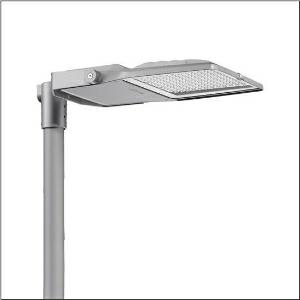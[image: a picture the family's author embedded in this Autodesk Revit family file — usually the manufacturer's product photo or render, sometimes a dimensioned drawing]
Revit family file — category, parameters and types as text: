
# Revit family: floodlight_fl_21_iq_midi___pl52_5xa7782e4d3a_8c54
name_source: partatom
category: Lighting Fixtures
units: mm (PartAtom-declared; Revit-internal decimal feet)

## family parameters
Cut with Voids When Loaded = No
Host = Face
Light Source = No
Part Type = Normal
Room Calculation Point = No
Round Connector Dimension = Use Diameter
Shared = No

## types (1)
- --- (1 x LED, 28010 lm, 208.1 W, 4000K)
    Apparent Load = 208 VA
    CIE Flux Codes = 26 60 98 100 100
    Color Rendering = 70
    Color Temperature = 4000K
    Default Elevation = 1800 mm
    Description = Floodlight FL 21 iQ midi, floodlight, primary light control with lens, of PMMA, primary optical cover: protective disc, of toughened safety glass, transparent, light distribution: PL52, light emission: direct distribution, installation type: surface-mounted, LED, High Power LED, rated luminous flux: 28.010lm, luminous efficacy: 135lm/W, light colour: 740, colour temperature: 4000K, control gear: iQ Street-Remote/DALI, control: optimised constant luminous flux control (CLO 2.0), Desk-Remote (wireless, voltage-free reading and setting of iQ features in the workshop via application-optimized NFC function/RFID function), Smart-Wire, Night-Set, Temp-Guard, Auto-Match, Street-Remote, with terminal, 6-pole, mains connection: 220..240V, AC, 50/60Hz, start of lifetime: 208W, end of service life: 227W, reduction: 90W, luminaire housing, of diecast aluminium, powder-coated, Siteco® metallic grey (DB 702S), corrosivity category C5 mid according to DIN EN ISO 12944, suitable for swimming pools, chlorine-resistant, sealing non-destructively replaceable, please order mast flange separately, mast bracket, of steel, galvanised, powder-coated, Siteco® metallic grey (DB 702S), protection rating (complete): IP66, insulation class (complete): insulation class II (safety insulation), certification: CE, ENEC, VDE, protection symbol: D, impact resistance: IK08, permissible operating ambient temperature: -40..+40°C, permissible operating ambient temperature for outdoor applications: -40..+50°C, standard: DIN EN 12944, LABS conformity tested according to VDMA 24364:2018-05, packaging unit: 1 piece

Light Distribution: PL52
    Height = 76 mm
    Lamp = 1 x LED
    Lamp Light Flux = 28010 lm
    Lamp Power = 208.1 W
    Lamp count = 1
    Length = 657 mm
    Luminous efficacy = 135 lm/W
    Manufacturer = Siteco
    ModVariant = No
    Model = 5XA7782E4D3A
    Number of Poles = 1
    OnlyDefault = Yes
    Power Factor = 1
    Product Name = Floodlight FL 21 iQ midi | PL52
    Product group = floodlight | pylon annexe
    ProductGroupID = 6200
    Protection Class = Protection class II
    Protection Degree = IP 66
    RLX_Detail_Level = 1
    RLX_Emergency_Light_Flux = 0 lm
    RLX_Emergency_Type = 0
    RLX_Emergency_Type_DB = No
    RlxData = <blob elided: 153909 chars, md5=d2919c9b>
    Socket = socket
    Standby Power = 0 W
    System Light Flux = 28010 lm
    System Power = 208 W
    Type Comments = factory setting: luminous flux: 100 % | dim-lin: 254 | 710 mA
    Type Image = l_1007123.jpg
    URL = http://relux.com
    VarID = @adj_105972
    Voltage = 0 V
    Weight = 0.00 kg
    Width = 442 mm

## geometry (parser evidence)
native form markers: Blend x4, Sweep x12
no freeform markers — native parametric forms only
